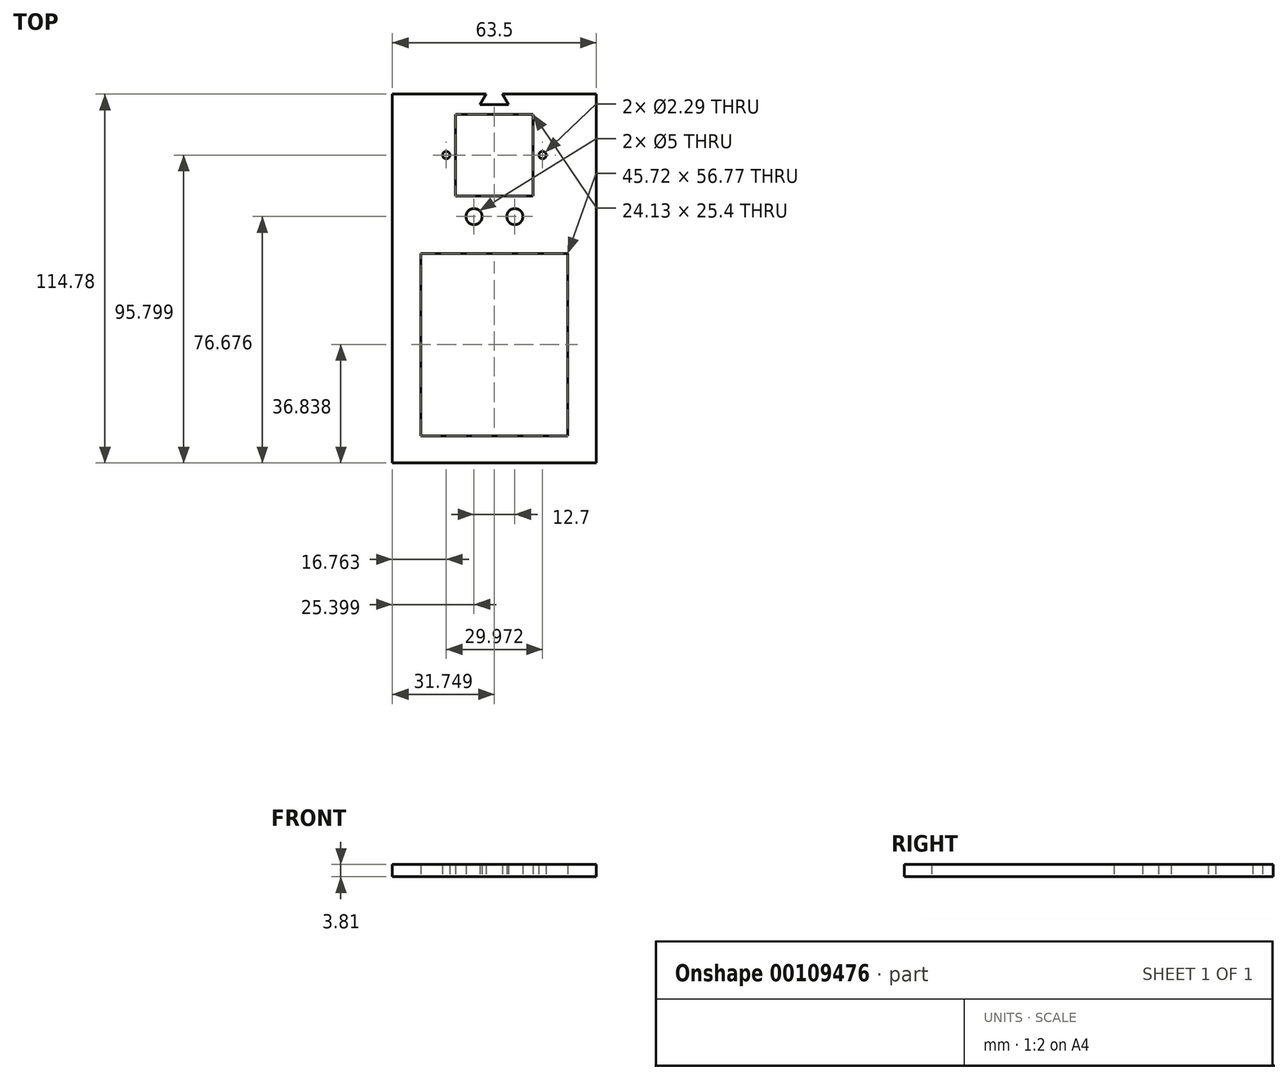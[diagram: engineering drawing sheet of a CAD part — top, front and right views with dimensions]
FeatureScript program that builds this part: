
annotation { "Feature Type Name" : "Feature", "Feature Type Description" : "" }
export const myFeature = defineFeature(function(context is Context, id is Id, definition is map)
    precondition{}
    {
        {
            var Q0;
            Q0=qCreatedBy(makeId("Top.planeOp"),FACE);
            var sketch = newSketch(context, id + "F0", { "sketchPlane" : qUnion([Q0])});
            skLineSegment(sketch, "E0.bottom", {"start": v(-17.4, 41.87) * mm, "end": v(5.47, 41.87) * mm});
            skLineSegment(sketch, "E1", {"start": v(6.94, 3.77) * mm, "end": v(14.36, 3.77) * mm, "construction": true});
            skLineSegment(sketch, "E2", {"start": v(6.94, 3.77) * mm, "end": v(1.66, 3.77) * mm, "construction": true});
            skCircle(sketch, "E3", {"center": v(1.66, 3.77) * mm, "radius": 2.5 * mm});
            skCircle(sketch, "E4", {"center": v(14.36, 3.77) * mm, "radius": 2.5 * mm});
            skLineSegment(sketch, "E5", {"start": v(5.47, 41.87) * mm, "end": v(3.56, 38.57) * mm});
            skLineSegment(sketch, "E6", {"start": v(10.55, 41.87) * mm, "end": v(12.45, 38.57) * mm});
            skLineSegment(sketch, "E7", {"start": v(3.56, 38.57) * mm, "end": v(12.45, 38.57) * mm});
            skLineSegment(sketch, "E8.trimOffspring", {"start": v(10.55, 41.87) * mm, "end": v(33.4, 41.87) * mm});
            skPoint(sketch, "E9.orphan", {"position": v(8, 41.87) * mm});
            skLineSegment(sketch, "E10", {"start": v(-4.06, 35.59) * mm, "end": v(20.07, 35.59) * mm});
            skLineSegment(sketch, "E11", {"start": v(-4.06, 35.59) * mm, "end": v(-4.06, 10.19) * mm});
            skLineSegment(sketch, "E12", {"start": v(-4.06, 10.19) * mm, "end": v(20.07, 10.19) * mm});
            skLineSegment(sketch, "E13", {"start": v(20.07, 10.19) * mm, "end": v(20.07, 35.59) * mm});
            skLineSegment(sketch, "E14", {"start": v(8, 41.87) * mm, "end": v(8, 3.77) * mm, "construction": true});
            skPoint(sketch, "E14.endSnap0", {"position": v(8, 10.19) * mm});
            skPoint(sketch, "E15", {"position": v(-4.06, 22.89) * mm});
            skLineSegment(sketch, "E16", {"start": v(-4.06, 22.89) * mm, "end": v(8, 22.89) * mm, "construction": true});
            skLineSegment(sketch, "E17", {"start": v(8, 22.89) * mm, "end": v(23, 22.89) * mm, "construction": true});
            skLineSegment(sketch, "E18", {"start": v(8, 22.89) * mm, "end": v(-6.98, 22.89) * mm, "construction": true});
            skCircle(sketch, "E19", {"center": v(23, 22.89) * mm, "radius": 1.14 * mm});
            skCircle(sketch, "E20", {"center": v(-6.98, 22.89) * mm, "radius": 1.14 * mm});
            skLineSegment(sketch, "E21", {"start": v(33.4, 41.87) * mm, "end": v(39.76, 41.87) * mm});
            skLineSegment(sketch, "E22", {"start": v(-17.4, 41.87) * mm, "end": v(-23.74, 41.87) * mm});
            skLineSegment(sketch, "E23", {"start": v(-23.74, 41.87) * mm, "end": v(-23.74, -47.5) * mm});
            skLineSegment(sketch, "E24", {"start": v(-23.74, -47.5) * mm, "end": v(-23.74, -72.9) * mm});
            skLineSegment(sketch, "E25", {"start": v(-23.74, -72.9) * mm, "end": v(39.76, -72.9) * mm});
            skLineSegment(sketch, "E26", {"start": v(39.76, 41.87) * mm, "end": v(39.76, -72.9) * mm});
            skLineSegment(sketch, "E27", {"start": v(-23.74, -7.69) * mm, "end": v(-14.85, -7.69) * mm, "construction": true});
            skLineSegment(sketch, "E28", {"start": v(-14.85, -7.69) * mm, "end": v(30.87, -7.69) * mm});
            skLineSegment(sketch, "E29", {"start": v(30.87, -7.69) * mm, "end": v(30.87, -64.46) * mm});
            skLineSegment(sketch, "E30", {"start": v(30.87, -64.46) * mm, "end": v(-14.85, -64.46) * mm});
            skLineSegment(sketch, "E31", {"start": v(-14.85, -64.46) * mm, "end": v(-14.85, -7.69) * mm});
            skSolve(sketch);
        }
        {
            var Q0;
            Q0=makeQuery(id+"F0.imprint","IMPRINT",FACE,{"disambiguationData":[TD([[makeQuery(id+"F0.imprint","IMPRINT",EDGE,{"derivedFrom":sQuery(id+"F0.wireOp",EDGE,"E0.bottom")}),-1.0]])]});
            extrude(context, id + "F1", {"entities" : qUnion([Q0]), "depth" : 3.8 * mm});
        }
    });
